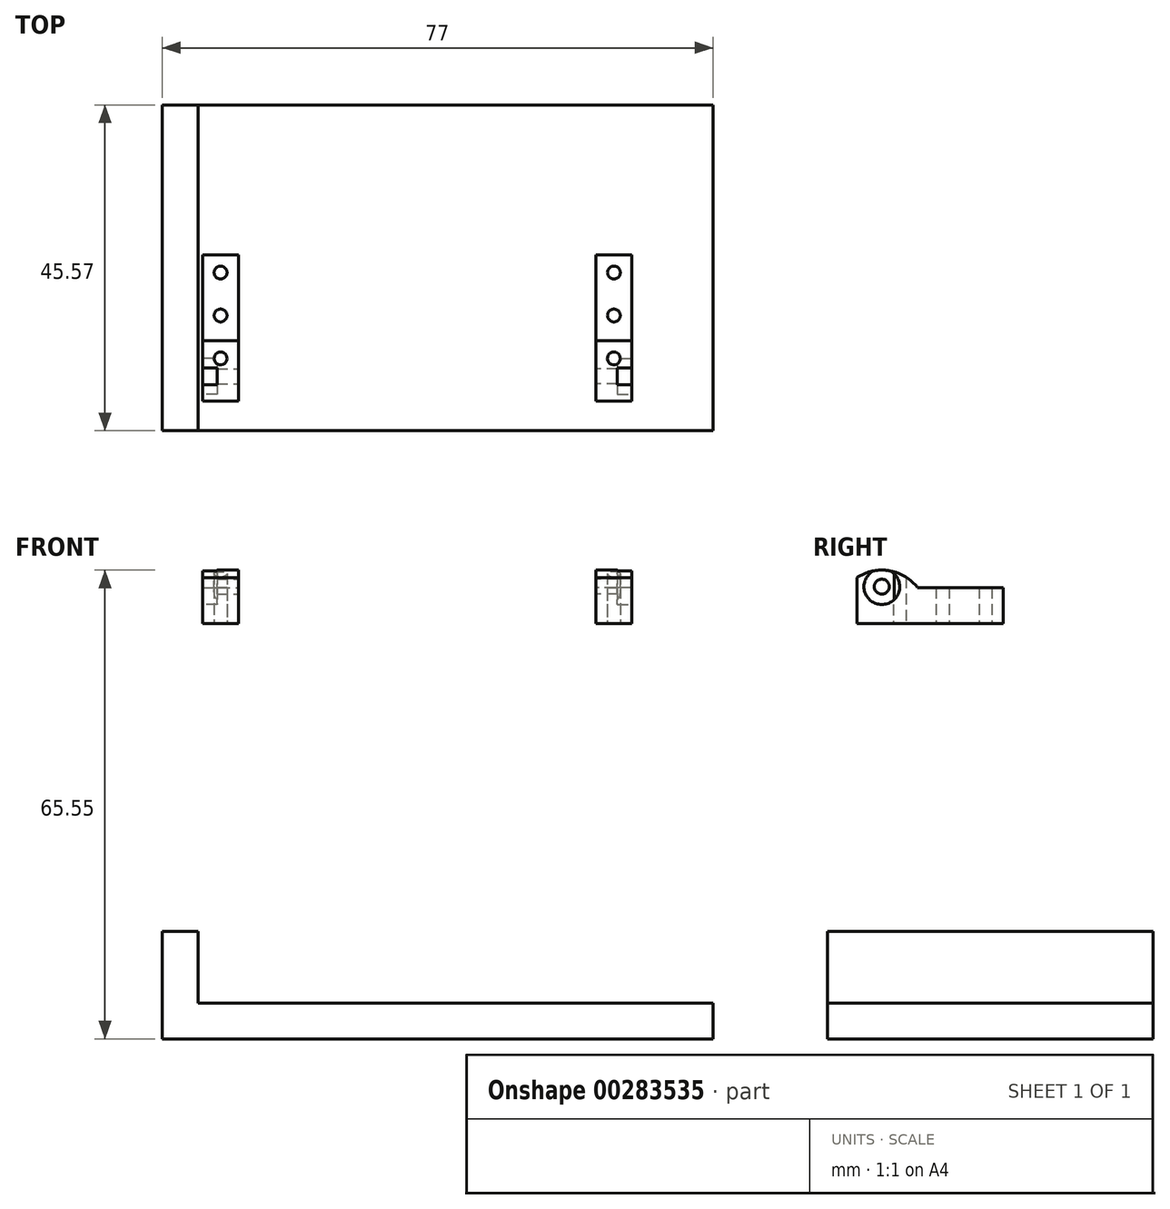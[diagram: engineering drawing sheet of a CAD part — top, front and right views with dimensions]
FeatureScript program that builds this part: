
annotation { "Feature Type Name" : "Feature", "Feature Type Description" : "" }
export const myFeature = defineFeature(function(context is Context, id is Id, definition is map)
    precondition{}
    {
        {
            var Q0;
            Q0=qCreatedBy(makeId("Right.planeOp"),FACE);
            var sketch = newSketch(context, id + "F0", { "sketchPlane" : qUnion([Q0])});
            skCircle(sketch, "E0", {"center": v(-37.95, 11.5) * mm, "radius": 1.05 * mm});
            skLineSegment(sketch, "E1", {"start": v(-41.43, 11.36) * mm, "end": v(-32.95, 11.36) * mm, "construction": true});
            skLineSegment(sketch, "E2", {"start": v(-37.95, 11.5) * mm, "end": v(-37.95, 7.5) * mm, "construction": true});
            skArc(sketch, "E3", {"start": v(-41.43, 12.77) * mm, "mid": v(-36.92, 13.73) * mm, "end": v(-32.95, 11.36) * mm});
            skLineSegment(sketch, "E4", {"start": v(-41.43, 6.36) * mm, "end": v(-32.95, 6.36) * mm});
            skLineSegment(sketch, "E5", {"start": v(-41.43, 12.77) * mm, "end": v(-41.43, 6.36) * mm});
            skLineSegment(sketch, "E6", {"start": v(-32.95, 11.36) * mm, "end": v(-32.95, 6.36) * mm});
            skSolve(sketch);
        }
        {
            var Q0;
            Q0=makeQuery(id+"F0.imprint","IMPRINT",FACE,{"disambiguationData":[TD([[makeQuery(id+"F0.imprint","IMPRINT",EDGE,{"derivedFrom":sQuery(id+"F0.wireOp",EDGE,"E0")}),-1.0]])]});
            extrude(context, id + "F1", {"entities" : qUnion([Q0]), "depth" : 5 * mm});
        }
        {
            var Q0;
            Q0=qCreatedBy(makeId("Right.planeOp"),FACE);
            cPlane(context, id + "F2", {"entities" : qUnion([Q0]), "cplaneType" : CPlaneType.OFFSET, "offset" : 25 * mm, "oppositeDirection" : true, "width" : 150 * mm, "height" : 150 * mm});
        }
        {
            var Q0;
            {var subQ0=sQuery(id+"F0.wireOp",EDGE,"E6");Q0=makeQuery(id+"Fr6NgedFq2PZrJn_1.boolean.opBoolean","MERGE",FACE,{"derivedFrom":[makeQuery(id+"F1.opExtrude","SWEPT_FACE",FACE,{"disambiguationData":[OSD([subQ0])]}),makeQuery(id+"Fr6NgedFq2PZrJn_1.opExtrude","SWEPT_FACE",FACE,{"disambiguationData":[OSD([subQ0])]})]});}
            extrude(context, id + "F3", {"entities" : qUnion([Q0]), "operationType" : NewBodyOperationType.ADD, "depth" : 12 * mm});
        }
        {
            var Q0;
            {var subQ0=sQuery(id+"F0.wireOp",EDGE,"E4");Q0=makeQuery(id+"Fr6NgedFq2PZrJn_1.boolean.opBoolean","MERGE",FACE,{"derivedFrom":[makeQuery(id+"F1.opExtrude","SWEPT_FACE",FACE,{"disambiguationData":[OSD([subQ0])]}),makeQuery(id+"Fr6NgedFq2PZrJn_1.opExtrude","SWEPT_FACE",FACE,{"disambiguationData":[OSD([subQ0])]})]});}
            var sketch = newSketch(context, id + "F4", { "sketchPlane" : qUnion([Q0])});
            skLineSegment(sketch, "E7", {"start": v(2.5, 20.95) * mm, "end": v(2.5, 41.43) * mm, "construction": true});
            skCircle(sketch, "E8", {"center": v(2.5, 29.45) * mm, "radius": 0.9 * mm});
            skCircle(sketch, "E9", {"center": v(2.5, 23.45) * mm, "radius": 0.9 * mm});
            skCircle(sketch, "E10", {"center": v(2.5, 35.45) * mm, "radius": 0.9 * mm});
            skSolve(sketch);
        }
        {
            var Q0;
            Q0=makeQuery(id+"F4.imprint","IMPRINT",FACE,{"disambiguationData":[TD([[makeQuery(id+"F4.imprint","IMPRINT",EDGE,{"derivedFrom":sQuery(id+"F4.wireOp",EDGE,"E10")}),1.0]])]});
            var Q1;
            Q1=makeQuery(id+"F4.imprint","IMPRINT",FACE,{"disambiguationData":[TD([[makeQuery(id+"F4.imprint","IMPRINT",EDGE,{"derivedFrom":sQuery(id+"F4.wireOp",EDGE,"E8")}),1.0]])]});
            var Q2;
            Q2=makeQuery(id+"F4.imprint","IMPRINT",FACE,{"disambiguationData":[TD([[makeQuery(id+"F4.imprint","IMPRINT",EDGE,{"derivedFrom":sQuery(id+"F4.wireOp",EDGE,"E9")}),1.0]])]});
            extrude(context, id + "F5", {"entities" : qUnion([Q0, Q1, Q2]), "operationType" : NewBodyOperationType.REMOVE, "endBound" : BoundingType.THROUGH_ALL, "oppositeDirection" : true, "depth" : 3 * mm});
        }
        {
            var Q0;
            {var subQ0=sQuery(id+"F0.wireOp",EDGE,"E6");Q0=makeQuery(id+"F3.boolean.opBoolean","MERGE",FACE,{"derivedFrom":[makeQuery(id+"F1.opExtrude","CAP_FACE",FACE,{"disambiguationData":[OSD([sQuery(id+"F0.wireOp",EDGE,"E0"),sQuery(id+"F0.wireOp",EDGE,"E3"),sQuery(id+"F0.wireOp",EDGE,"E4"),sQuery(id+"F0.wireOp",EDGE,"E5"),subQ0])],"isStart":false}),makeQuery(id+"F3.opExtrude","SWEPT_FACE",FACE,{"disambiguationData":[OSD([subQ0]),TDD([makeQuery(id+"F1.opExtrude","CAP_EDGE",EDGE,{"disambiguationData":[OSD([subQ0])],"isStart":false})])]})]});}
            var sketch = newSketch(context, id + "F6", { "sketchPlane" : qUnion([Q0])});
            skCircle(sketch, "E11", {"center": v(-37.95, 11.5) * mm, "radius": 2.5 * mm});
            skSolve(sketch);
        }
        {
            var Q0;
            Q0=makeQuery(id+"F6.imprint","IMPRINT",FACE,{"disambiguationData":[TD([[makeQuery(id+"F6.imprint","IMPRINT",EDGE,{"derivedFrom":makeQuery(id+"F1.opExtrude","CAP_EDGE",EDGE,{"disambiguationData":[OSD([sQuery(id+"F0.wireOp",EDGE,"E0")])],"isStart":false})}),-1.0]])]});
            extrude(context, id + "F7", {"entities" : qUnion([Q0]), "operationType" : NewBodyOperationType.REMOVE, "oppositeDirection" : true, "depth" : 2 * mm});
        }
        {
            var Q0;
            Q0=makeQuery(id+"F1.opExtrude","SWEPT_BODY",BODY,{"disambiguationData":[OSD([sQuery(id+"F0.wireOp",EDGE,"E0"),sQuery(id+"F0.wireOp",EDGE,"E3"),sQuery(id+"F0.wireOp",EDGE,"E4"),sQuery(id+"F0.wireOp",EDGE,"E5"),sQuery(id+"F0.wireOp",EDGE,"E6")])]});
            var Q1;
            Q1=qCreatedBy(id+"F2.planeOp",FACE);
            mirror(context, id + "F8", {"entities" : qUnion([Q0]), "mirrorPlane" : qUnion([Q1])});
        }
        {
            var Q0;
            Q0=qCreatedBy(makeId("Front.planeOp"),FACE);
            var sketch = newSketch(context, id + "F9", { "sketchPlane" : qUnion([Q0])});
            skLineSegment(sketch, "E12.bottom", {"start": v(-55.65, -46.74) * mm, "end": v(16.35, -46.74) * mm});
            skLineSegment(sketch, "E12.left", {"start": v(-55.65, -46.74) * mm, "end": v(-55.65, -36.74) * mm});
            skLineSegment(sketch, "E13.top", {"start": v(-55.65, -36.74) * mm, "end": v(-60.65, -36.74) * mm});
            skLineSegment(sketch, "E13.right", {"start": v(-60.65, -46.74) * mm, "end": v(-60.65, -36.74) * mm});
            skLineSegment(sketch, "E14.top", {"start": v(-60.65, -51.74) * mm, "end": v(16.35, -51.74) * mm});
            skLineSegment(sketch, "E14.left", {"start": v(-60.65, -46.74) * mm, "end": v(-60.65, -51.74) * mm});
            skLineSegment(sketch, "E14.right", {"start": v(16.35, -46.74) * mm, "end": v(16.35, -51.74) * mm});
            skSolve(sketch);
        }
        {
            var Q0;
            Q0=makeQuery(id+"F9.imprint","IMPRINT",FACE,{"disambiguationData":[TD([[makeQuery(id+"F9.imprint","IMPRINT",EDGE,{"derivedFrom":sQuery(id+"F9.wireOp",EDGE,"E13.top")}),1.0]])]});
            extrude(context, id + "F10", {"entities" : qUnion([Q0]), "depth" : 45.57 * mm});
        }
    });
